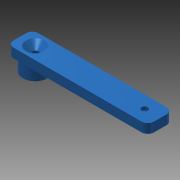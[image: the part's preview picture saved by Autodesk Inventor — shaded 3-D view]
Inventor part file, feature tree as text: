
AUTODESK INVENTOR PART (.ipt)
format: ipt  version: 2013 (Build 170138000, 138)  size: 105,984 bytes
history: native  units: mm
features: extrude x2, sketch x2, fillet x1, chamfer x1
ambient origin geometry x8: Origin, YZ Plane, XZ Plane, XY Plane, X Axis, Y Axis, Z Axis, Center Point
bodies: Solid1 (feature_tree)
feature tree (6):
  extrude  "Extrusion1"  Depth=8.0mm
  fillet  "Fillet1"  Radius=2.0mm
  chamfer  "Chamfer1"  Distance=5.0mm
  extrude  "Extrusion2"  Depth=5.0mm
  sketch  "Sketch1"  dims[d0=45.0mm d1=8.0mm d2=2.0mm]
  sketch  "Sketch2"  dims[d3=2.0mm d4=5.0mm d5=5.0mm d6=3.0mm d7=0.0mm d8=2.0mm d9=2.0mm d10=2.0mm d11=45.0deg d12=8.0mm d13=4.0mm d14=0.0mm]
